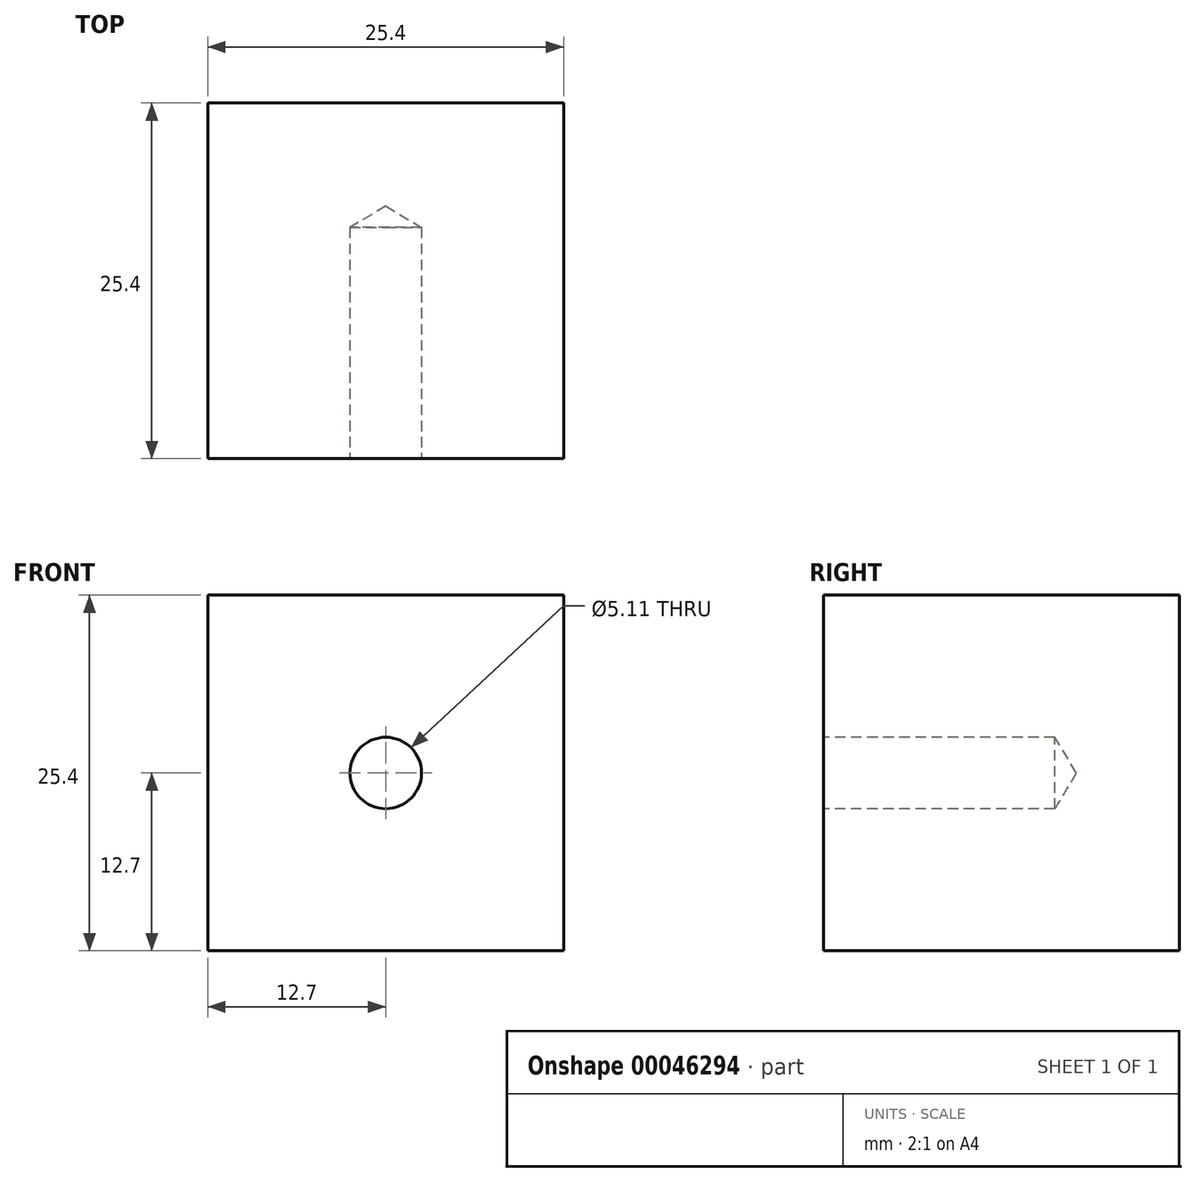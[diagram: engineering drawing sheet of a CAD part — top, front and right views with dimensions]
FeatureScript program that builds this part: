
annotation { "Feature Type Name" : "Feature", "Feature Type Description" : "" }
export const myFeature = defineFeature(function(context is Context, id is Id, definition is map)
    precondition{}
    {
        {
            var Q0;
            Q0=qCreatedBy(makeId("Front.planeOp"),FACE);
            var sketch = newSketch(context, id + "F0", { "sketchPlane" : qUnion([Q0])});
            skLineSegment(sketch, "E0.rect.bottom", {"start": v(12.7, 12.7) * mm, "end": v(-12.7, 12.7) * mm});
            skLineSegment(sketch, "E0.rect.top", {"start": v(12.7, -12.7) * mm, "end": v(-12.7, -12.7) * mm});
            skLineSegment(sketch, "E0.rect.left", {"start": v(12.7, 12.7) * mm, "end": v(12.7, -12.7) * mm});
            skLineSegment(sketch, "E0.rect.right", {"start": v(-12.7, 12.7) * mm, "end": v(-12.7, -12.7) * mm});
            skPoint(sketch, "E0.rect.middle", {"position": v(0, 0) * mm});
            skSolve(sketch);
        }
        {
            var Q0;
            Q0=makeQuery(id+"F0.imprint","IMPRINT",FACE,{"disambiguationData":[TD([[makeQuery(id+"F0.imprint","IMPRINT",EDGE,{"derivedFrom":sQuery(id+"F0.wireOp",EDGE,"E0.rect.bottom")}),1.0]])]});
            extrude(context, id + "F1", {"entities" : qUnion([Q0]), "endBound" : BoundingType.SYMMETRIC, "depth" : 25.4 * mm});
        }
        {
            var Q0;
            Q0=makeQuery(id+"F1.opExtrude","CAP_FACE",FACE,{"disambiguationData":[OSD([sQuery(id+"F0.wireOp",EDGE,"E0.rect.bottom"),sQuery(id+"F0.wireOp",EDGE,"E0.rect.top"),sQuery(id+"F0.wireOp",EDGE,"E0.rect.left"),sQuery(id+"F0.wireOp",EDGE,"E0.rect.right")])],"isStart":false});
            var sketch = newSketch(context, id + "F2", { "sketchPlane" : qUnion([Q0])});
            skPoint(sketch, "E1", {"position": v(0, 0) * mm});
            skSolve(sketch);
        }
        {
            var Q0;
            Q0=sQuery(id+"F2.wireOp",VERTEX,"E1");
            var Q1;
            Q1=makeQuery(id+"F1.opExtrude","SWEPT_BODY",BODY,{"disambiguationData":[OSD([sQuery(id+"F0.wireOp",EDGE,"E0.rect.bottom"),sQuery(id+"F0.wireOp",EDGE,"E0.rect.top"),sQuery(id+"F0.wireOp",EDGE,"E0.rect.left"),sQuery(id+"F0.wireOp",EDGE,"E0.rect.right")])]});
            hole(context, id + "F3", {"style" : HoleStyle.SIMPLE, "holeDiameter" : 5.1 * mm, "endStyle" : HoleEndStyle.BLIND, "standardTappedOrClearance" : lookupTablePath({ "standard" : "ANSI", "fit" : "Normal (ASME)", "engagement" : "75%", "pitch" : "20 tpi", "size" : "1/4", "type" : "Tapped" }), "standardBlindInLast" : lookupTablePath({ "fit" : "Normal", "standard" : "ANSI", "engagement" : "75%", "pitch" : "20 tpi", "size" : "1/4", "type" : "Clearance & tapped" }), "holeDepth" : 16.51 * mm, "locations" : qUnion([Q0]), "scope" : qUnion([Q1]), "majorDiameter" : 6.35 * mm, "showTappedDepth" : true, "tappedDepth" : 12.7 * mm, "tapClearance" : 3});
        }
    });
